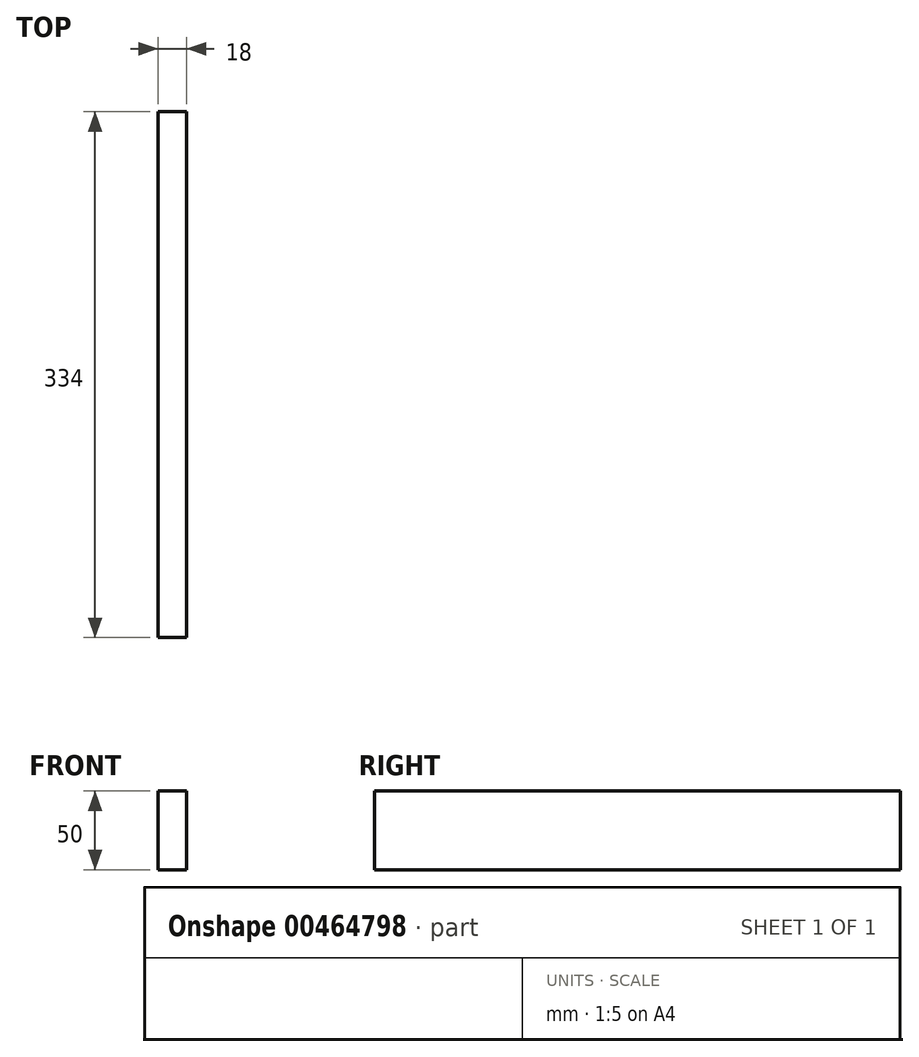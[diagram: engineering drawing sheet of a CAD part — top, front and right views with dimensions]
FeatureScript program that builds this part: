
annotation { "Feature Type Name" : "Feature", "Feature Type Description" : "" }
export const myFeature = defineFeature(function(context is Context, id is Id, definition is map)
    precondition{}
    {
        {
            var Q0;
            Q0=qCreatedBy(makeId("Right.planeOp"),FACE);
            var sketch = newSketch(context, id + "F0", { "sketchPlane" : qUnion([Q0])});
            skLineSegment(sketch, "E0.bottom", {"start": v(0, 0) * mm, "end": v(334, 0) * mm});
            skLineSegment(sketch, "E0.top", {"start": v(0, 50) * mm, "end": v(334, 50) * mm});
            skLineSegment(sketch, "E0.left", {"start": v(0, 0) * mm, "end": v(0, 50) * mm});
            skLineSegment(sketch, "E0.right", {"start": v(334, 0) * mm, "end": v(334, 50) * mm});
            skSolve(sketch);
        }
        {
            var Q0;
            Q0=makeQuery(id+"F0.imprint","IMPRINT",FACE,{"disambiguationData":[TD([[makeQuery(id+"F0.imprint","IMPRINT",EDGE,{"derivedFrom":sQuery(id+"F0.wireOp",EDGE,"E0.bottom")}),1.0]])]});
            extrude(context, id + "F1", {"entities" : qUnion([Q0]), "depth" : 18 * mm});
        }
    });
